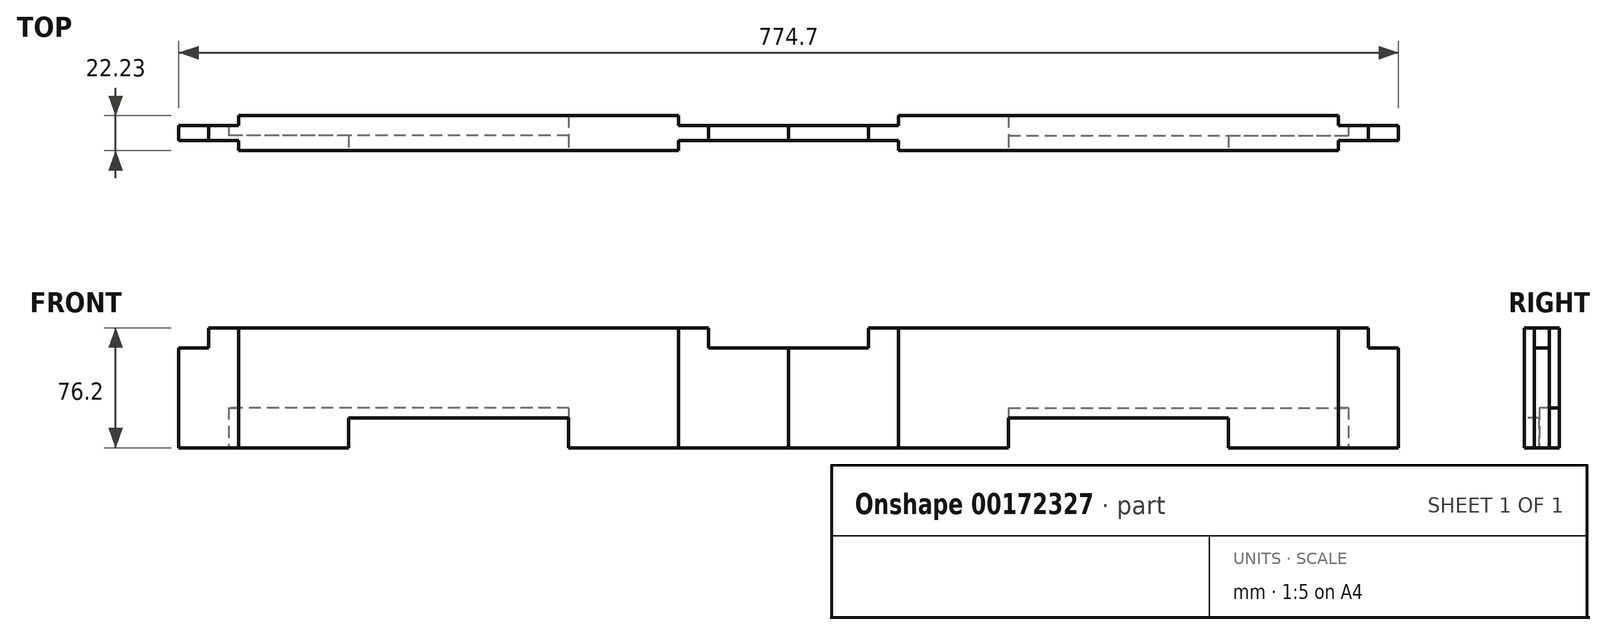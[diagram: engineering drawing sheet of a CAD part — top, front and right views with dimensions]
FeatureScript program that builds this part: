
annotation { "Feature Type Name" : "Feature", "Feature Type Description" : "" }
export const myFeature = defineFeature(function(context is Context, id is Id, definition is map)
    precondition{}
    {
        {
            var Q0;
            Q0=qCreatedBy(makeId("Front.planeOp"),FACE);
            var sketch = newSketch(context, id + "F0", { "sketchPlane" : qUnion([Q0])});
            skLineSegment(sketch, "E0.bottom", {"start": v(0, 0) * mm, "end": v(387.35, 0) * mm});
            skLineSegment(sketch, "E0.top", {"start": v(0, 76.2) * mm, "end": v(387.35, 76.2) * mm});
            skLineSegment(sketch, "E0.left", {"start": v(0, 0) * mm, "end": v(0, 76.2) * mm});
            skLineSegment(sketch, "E0.right", {"start": v(387.35, 0) * mm, "end": v(387.35, 76.2) * mm});
            skSolve(sketch);
        }
        {
            var Q0;
            Q0=makeQuery(id+"F0.imprint","IMPRINT",FACE,{"disambiguationData":[TD([[makeQuery(id+"F0.imprint","IMPRINT",EDGE,{"derivedFrom":sQuery(id+"F0.wireOp",EDGE,"E0.bottom")}),1.0]])]});
            extrude(context, id + "F1", {"entities" : qUnion([Q0]), "depth" : 22.22 * mm});
        }
        {
            var Q0;
            Q0=makeQuery(id+"F1.opExtrude","SWEPT_FACE",FACE,{"disambiguationData":[OSD([sQuery(id+"F0.wireOp",EDGE,"E0.bottom")])]});
            var sketch = newSketch(context, id + "F2", { "sketchPlane" : qUnion([Q0])});
            skLineSegment(sketch, "E1.bottom", {"start": v(0, 15.88) * mm, "end": v(387.35, 15.88) * mm});
            skLineSegment(sketch, "E1.top", {"start": v(0, 6.35) * mm, "end": v(387.35, 6.35) * mm});
            skLineSegment(sketch, "E1.left", {"start": v(0, 15.88) * mm, "end": v(0, 6.35) * mm});
            skLineSegment(sketch, "E1.right", {"start": v(387.35, 15.88) * mm, "end": v(387.35, 6.35) * mm});
            skLineSegment(sketch, "E2", {"start": v(69.85, 22.23) * mm, "end": v(69.85, 0) * mm});
            skLineSegment(sketch, "E3", {"start": v(349.25, 22.23) * mm, "end": v(349.25, 0) * mm});
            skSolve(sketch);
        }
        {
            var Q0;
            {var subQ1=sQuery(id+"F0.wireOp",EDGE,"E0.bottom");var subQ4=sQuery(id+"F2.wireOp",EDGE,"E2");var subQ6=makeQuery(id+"F1.opExtrude","CAP_EDGE",EDGE,{"disambiguationData":[OSD([subQ1])],"isStart":false});var subQ7=makeQuery(id+"F2.imprint","INTERSECT",VERTEX,{"derivedFrom":[subQ6,subQ4]});Q0=makeQuery(id+"F2.imprint","IMPRINT",FACE,{"disambiguationData":[TD([[makeQuery(id+"F2.imprint","IMPRINT",EDGE,{"disambiguationData":[TD([[subQ7,-1.0]])],"derivedFrom":subQ4}),-1.0]])]});}
            var Q1;
            {var subQ1=sQuery(id+"F0.wireOp",EDGE,"E0.bottom");var subQ4=sQuery(id+"F2.wireOp",EDGE,"E2");var subQ6=makeQuery(id+"F1.opExtrude","CAP_EDGE",EDGE,{"disambiguationData":[OSD([subQ1])],"isStart":true});var subQ7=makeQuery(id+"F2.imprint","INTERSECT",VERTEX,{"derivedFrom":[subQ6,subQ4]});Q1=makeQuery(id+"F2.imprint","IMPRINT",FACE,{"disambiguationData":[TD([[makeQuery(id+"F2.imprint","IMPRINT",EDGE,{"disambiguationData":[TD([[subQ7,1.0]])],"derivedFrom":subQ4}),-1.0]])]});}
            var Q2;
            {var subQ1=sQuery(id+"F0.wireOp",EDGE,"E0.bottom");var subQ4=sQuery(id+"F2.wireOp",EDGE,"E3");var subQ6=makeQuery(id+"F1.opExtrude","CAP_EDGE",EDGE,{"disambiguationData":[OSD([subQ1])],"isStart":false});var subQ7=makeQuery(id+"F2.imprint","INTERSECT",VERTEX,{"derivedFrom":[subQ6,subQ4]});Q2=makeQuery(id+"F2.imprint","IMPRINT",FACE,{"disambiguationData":[TD([[makeQuery(id+"F2.imprint","IMPRINT",EDGE,{"disambiguationData":[TD([[subQ7,-1.0]])],"derivedFrom":subQ4}),1.0]])]});}
            var Q3;
            {var subQ1=sQuery(id+"F0.wireOp",EDGE,"E0.bottom");var subQ4=sQuery(id+"F2.wireOp",EDGE,"E3");var subQ6=makeQuery(id+"F1.opExtrude","CAP_EDGE",EDGE,{"disambiguationData":[OSD([subQ1])],"isStart":true});var subQ7=makeQuery(id+"F2.imprint","INTERSECT",VERTEX,{"derivedFrom":[subQ6,subQ4]});Q3=makeQuery(id+"F2.imprint","IMPRINT",FACE,{"disambiguationData":[TD([[makeQuery(id+"F2.imprint","IMPRINT",EDGE,{"disambiguationData":[TD([[subQ7,1.0]])],"derivedFrom":subQ4}),1.0]])]});}
            extrude(context, id + "F3", {"entities" : qUnion([Q0, Q1, Q2, Q3]), "operationType" : NewBodyOperationType.REMOVE, "endBound" : BoundingType.UP_TO_NEXT, "oppositeDirection" : true, "depth" : 25.4 * mm});
        }
        {
            var Q0;
            {var subQ0=sQuery(id+"F2.wireOp",EDGE,"E1.bottom");Q0=makeQuery(id+"F3.boolean.opBoolean","COPY",FACE,{"derivedFrom":makeQuery(id+"F3.opExtrude","SWEPT_FACE",FACE,{"disambiguationData":[OSD([subQ0]),TDD([makeQuery(id+"F2.imprint","IMPRINT",EDGE,{"disambiguationData":[TD([[makeQuery(id+"F2.imprint","INTERSECT",VERTEX,{"derivedFrom":[subQ0,sQuery(id+"F2.wireOp",EDGE,"E2")]}),1.0]])],"derivedFrom":subQ0})])]})});}
            var sketch = newSketch(context, id + "F4", { "sketchPlane" : qUnion([Q0])});
            skLineSegment(sketch, "E4.bottom", {"start": v(0, 76.2) * mm, "end": v(50.8, 76.2) * mm});
            skLineSegment(sketch, "E4.top", {"start": v(0, 63.5) * mm, "end": v(50.8, 63.5) * mm});
            skLineSegment(sketch, "E4.left", {"start": v(0, 76.2) * mm, "end": v(0, 63.5) * mm});
            skLineSegment(sketch, "E4.right", {"start": v(50.8, 76.2) * mm, "end": v(50.8, 63.5) * mm});
            skLineSegment(sketch, "E5.bottom", {"start": v(368.3, 63.5) * mm, "end": v(387.35, 63.5) * mm});
            skLineSegment(sketch, "E5.top", {"start": v(368.3, 76.2) * mm, "end": v(387.35, 76.2) * mm});
            skLineSegment(sketch, "E5.left", {"start": v(368.3, 63.5) * mm, "end": v(368.3, 76.2) * mm});
            skLineSegment(sketch, "E5.right", {"start": v(387.35, 63.5) * mm, "end": v(387.35, 76.2) * mm});
            skSolve(sketch);
        }
        {
            var Q0;
            Q0=makeQuery(id+"F4.imprint","IMPRINT",FACE,{"disambiguationData":[TD([[makeQuery(id+"F4.imprint","IMPRINT",EDGE,{"derivedFrom":sQuery(id+"F4.wireOp",EDGE,"E4.bottom")}),-1.0]])]});
            var Q1;
            Q1=makeQuery(id+"F4.imprint","IMPRINT",FACE,{"disambiguationData":[TD([[makeQuery(id+"F4.imprint","IMPRINT",EDGE,{"derivedFrom":sQuery(id+"F4.wireOp",EDGE,"E5.bottom")}),1.0]])]});
            extrude(context, id + "F5", {"entities" : qUnion([Q0, Q1]), "operationType" : NewBodyOperationType.REMOVE, "endBound" : BoundingType.UP_TO_NEXT, "oppositeDirection" : true, "depth" : 25.4 * mm});
        }
        {
            var Q0;
            Q0=makeQuery(id+"F1.opExtrude","CAP_FACE",FACE,{"disambiguationData":[OSD([sQuery(id+"F0.wireOp",EDGE,"E0.bottom"),sQuery(id+"F0.wireOp",EDGE,"E0.top"),sQuery(id+"F0.wireOp",EDGE,"E0.left"),sQuery(id+"F0.wireOp",EDGE,"E0.right")])],"isStart":false});
            var sketch = newSketch(context, id + "F6", { "sketchPlane" : qUnion([Q0])});
            skLineSegment(sketch, "E6.bottom", {"start": v(139.7, 0) * mm, "end": v(279.4, 0) * mm});
            skLineSegment(sketch, "E6.top", {"start": v(139.7, 19.05) * mm, "end": v(279.4, 19.05) * mm});
            skLineSegment(sketch, "E6.left", {"start": v(139.7, 0) * mm, "end": v(139.7, 19.05) * mm});
            skLineSegment(sketch, "E6.right", {"start": v(279.4, 0) * mm, "end": v(279.4, 19.05) * mm});
            skSolve(sketch);
        }
        {
            var Q0;
            Q0=makeQuery(id+"F6.imprint","IMPRINT",FACE,{"disambiguationData":[TD([[makeQuery(id+"F6.imprint","IMPRINT",EDGE,{"derivedFrom":sQuery(id+"F6.wireOp",EDGE,"E6.bottom")}),1.0]])]});
            extrude(context, id + "F7", {"entities" : qUnion([Q0]), "operationType" : NewBodyOperationType.REMOVE, "endBound" : BoundingType.UP_TO_NEXT, "oppositeDirection" : true, "depth" : 25.4 * mm});
        }
        {
            var Q0;
            {var subQ2=sQuery(id+"F0.wireOp",EDGE,"E0.left");var subQ3=sQuery(id+"F0.wireOp",EDGE,"E0.bottom");Q0=makeQuery(id+"F7.boolean.opBoolean","SPLIT",FACE,{"disambiguationData":[TD([makeQuery(id+"F1.opExtrude","SWEPT_FACE",FACE,{"disambiguationData":[OSD([subQ2])]})])],"derivedFrom":makeQuery(id+"F1.opExtrude","SWEPT_FACE",FACE,{"disambiguationData":[OSD([subQ3])]})});}
            var sketch = newSketch(context, id + "F8", { "sketchPlane" : qUnion([Q0])});
            skLineSegment(sketch, "E7.bottom", {"start": v(63.5, 0) * mm, "end": v(355.6, 0) * mm});
            skLineSegment(sketch, "E7.top", {"start": v(63.5, 12.7) * mm, "end": v(355.6, 12.7) * mm});
            skLineSegment(sketch, "E7.left", {"start": v(63.5, 0) * mm, "end": v(63.5, 12.7) * mm});
            skLineSegment(sketch, "E7.right", {"start": v(355.6, 0) * mm, "end": v(355.6, 12.7) * mm});
            skSolve(sketch);
        }
        {
            var Q0;
            {var subQ4=sQuery(id+"F0.wireOp",EDGE,"E0.bottom");var subQ5=sQuery(id+"F2.wireOp",EDGE,"E2");var subQ9=makeQuery(id+"F3.boolean.opBoolean","COPY",EDGE,{"derivedFrom":makeQuery(id+"F3.opExtrude","CAP_EDGE",EDGE,{"disambiguationData":[OSD([subQ5]),TDD([makeQuery(id+"F2.imprint","IMPRINT",EDGE,{"disambiguationData":[TD([[makeQuery(id+"F2.imprint","INTERSECT",VERTEX,{"derivedFrom":[makeQuery(id+"F1.opExtrude","CAP_EDGE",EDGE,{"disambiguationData":[OSD([subQ4])],"isStart":true}),subQ5]}),1.0]])],"derivedFrom":subQ5})])],"isStart":true})});Q0=makeQuery(id+"F8.imprint","IMPRINT",FACE,{"disambiguationData":[TD([[makeQuery(id+"F8.imprint","IMPRINT",EDGE,{"derivedFrom":subQ9}),1.0]])]});}
            var Q1;
            {var subQ3=sQuery(id+"F8.wireOp",EDGE,"E7.right");Q1=makeQuery(id+"F8.imprint","IMPRINT",FACE,{"disambiguationData":[TD([[makeQuery(id+"F8.imprint","IMPRINT",EDGE,{"derivedFrom":subQ3}),1.0]])]});}
            extrude(context, id + "F9", {"entities" : qUnion([Q0, Q1]), "operationType" : NewBodyOperationType.REMOVE, "oppositeDirection" : true, "depth" : 25.4 * mm});
        }
        {
            var Q0;
            Q0=makeQuery(id+"F1.opExtrude","SWEPT_BODY",BODY,{"disambiguationData":[OSD([sQuery(id+"F0.wireOp",EDGE,"E0.bottom"),sQuery(id+"F0.wireOp",EDGE,"E0.top"),sQuery(id+"F0.wireOp",EDGE,"E0.left"),sQuery(id+"F0.wireOp",EDGE,"E0.right")])]});
            var Q1;
            Q1=qCreatedBy(makeId("Right.planeOp"),FACE);
            mirror(context, id + "F10", {"entities" : qUnion([Q0]), "mirrorPlane" : qUnion([Q1])});
        }
    });
